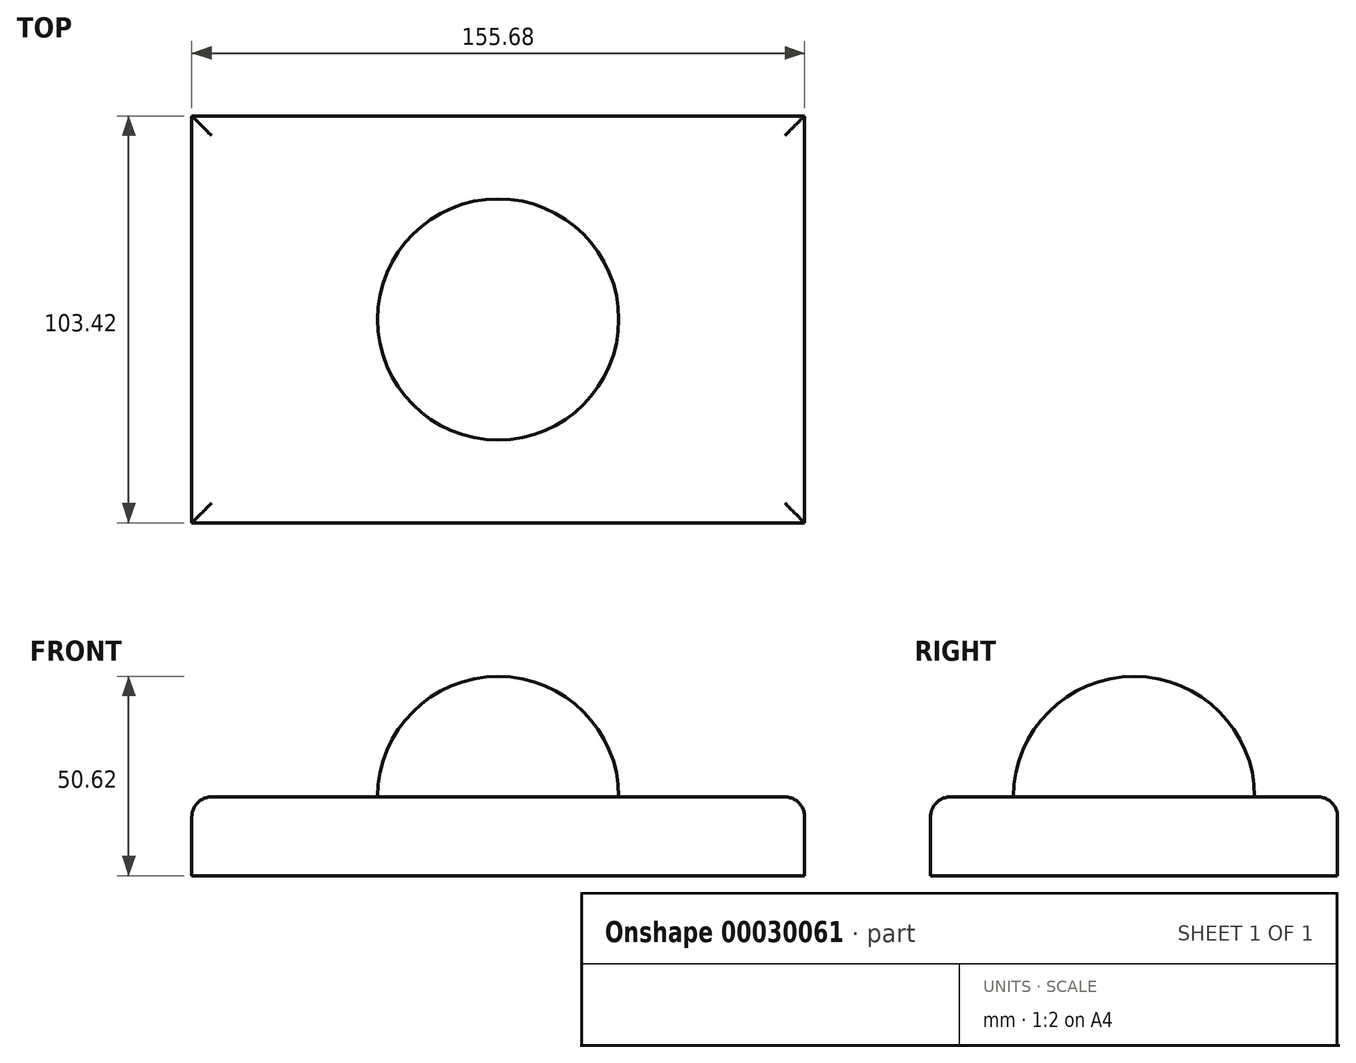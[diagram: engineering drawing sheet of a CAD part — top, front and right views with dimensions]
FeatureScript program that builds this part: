
annotation { "Feature Type Name" : "Feature", "Feature Type Description" : "" }
export const myFeature = defineFeature(function(context is Context, id is Id, definition is map)
    precondition{}
    {
        {
            var Q0;
            Q0=qCreatedBy(makeId("Top.planeOp"),FACE);
            var sketch = newSketch(context, id + "F0", { "sketchPlane" : qUnion([Q0])});
            skLineSegment(sketch, "E0.rect.bottom", {"start": v(77.84, 51.7) * mm, "end": v(-77.84, 51.7) * mm});
            skLineSegment(sketch, "E0.rect.top", {"start": v(77.84, -51.7) * mm, "end": v(-77.84, -51.7) * mm});
            skLineSegment(sketch, "E0.rect.left", {"start": v(77.84, 51.7) * mm, "end": v(77.84, -51.7) * mm});
            skLineSegment(sketch, "E0.rect.right", {"start": v(-77.84, 51.7) * mm, "end": v(-77.84, -51.7) * mm});
            skPoint(sketch, "E0.rect.middle", {"position": v(0, 0) * mm});
            skCircle(sketch, "E1", {"center": v(0, 0) * mm, "radius": 30.62 * mm});
            skLineSegment(sketch, "E2", {"start": v(0, -30.62) * mm, "end": v(0, 30.62) * mm});
            skSolve(sketch);
        }
        {
            var Q0;
            Q0=makeQuery(id+"F0.imprint","IMPRINT",FACE,{"disambiguationData":[TD([[makeQuery(id+"F0.imprint","IMPRINT",EDGE,{"derivedFrom":sQuery(id+"F0.wireOp",EDGE,"E0.rect.bottom")}),1.0]])]});
            var Q1;
            {var subQ0=sQuery(id+"F0.wireOp",EDGE,"E2");Q1=makeQuery(id+"F0.imprint","IMPRINT",FACE,{"disambiguationData":[TD([[makeQuery(id+"F0.imprint","IMPRINT",EDGE,{"derivedFrom":subQ0}),1.0]])]});}
            var Q2;
            {var subQ0=sQuery(id+"F0.wireOp",EDGE,"E2");Q2=makeQuery(id+"F0.imprint","IMPRINT",FACE,{"disambiguationData":[TD([[makeQuery(id+"F0.imprint","IMPRINT",EDGE,{"derivedFrom":subQ0}),-1.0]])]});}
            extrude(context, id + "F1", {"entities" : qUnion([Q0, Q1, Q2]), "oppositeDirection" : true, "depth" : 20 * mm});
        }
        {
            var Q0;
            {var subQ0=sQuery(id+"F0.wireOp",EDGE,"E2");Q0=makeQuery(id+"F0.imprint","IMPRINT",FACE,{"disambiguationData":[TD([[makeQuery(id+"F0.imprint","IMPRINT",EDGE,{"derivedFrom":subQ0}),-1.0]])]});}
            var Q1;
            Q1=sQuery(id+"F0.wireOp",EDGE,"E2");
            revolve(context, id + "F2", {"operationType" : NewBodyOperationType.ADD, "entities" : qUnion([Q0]), "axis" : qUnion([Q1]), "revolveType" : RevolveType.ONE_DIRECTION, "oppositeDirection" : true, "angle" : 180 * degree});
        }
        {
            var Q0;
            Q0=makeQuery(id+"F1.opExtrude","CAP_EDGE",EDGE,{"disambiguationData":[OSD([sQuery(id+"F0.wireOp",EDGE,"E0.rect.right")])],"isStart":true});
            var Q1;
            Q1=makeQuery(id+"F1.opExtrude","CAP_EDGE",EDGE,{"disambiguationData":[OSD([sQuery(id+"F0.wireOp",EDGE,"E0.rect.top")])],"isStart":true});
            var Q2;
            Q2=makeQuery(id+"F1.opExtrude","CAP_EDGE",EDGE,{"disambiguationData":[OSD([sQuery(id+"F0.wireOp",EDGE,"E0.rect.left")])],"isStart":true});
            var Q3;
            Q3=makeQuery(id+"F1.opExtrude","CAP_EDGE",EDGE,{"disambiguationData":[OSD([sQuery(id+"F0.wireOp",EDGE,"E0.rect.bottom")])],"isStart":true});
            fillet(context, id + "F3", {"entities" : qUnion([Q0, Q1, Q2, Q3]), "radius" : 5 * mm, "tangentPropagation" : true, "allowEdgeOverflow" : false});
        }
    });
